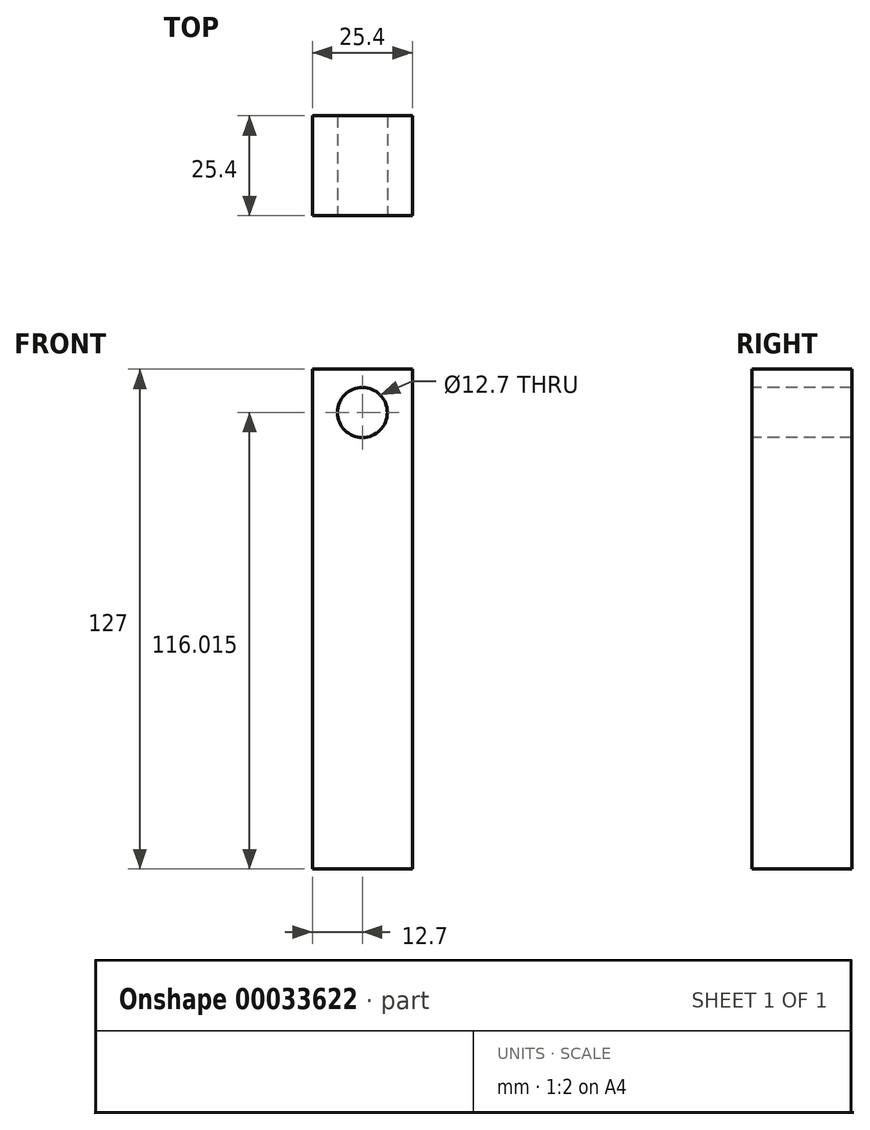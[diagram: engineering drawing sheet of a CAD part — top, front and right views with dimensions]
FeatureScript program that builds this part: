
annotation { "Feature Type Name" : "Feature", "Feature Type Description" : "" }
export const myFeature = defineFeature(function(context is Context, id is Id, definition is map)
    precondition{}
    {
        {
            var Q0;
            Q0=qCreatedBy(makeId("Top.planeOp"),FACE);
            var sketch = newSketch(context, id + "F0", { "sketchPlane" : qUnion([Q0])});
            skLineSegment(sketch, "E0.bottom", {"start": v(0, 0) * mm, "end": v(25.4, 0) * mm});
            skLineSegment(sketch, "E0.top", {"start": v(0, 25.4) * mm, "end": v(25.4, 25.4) * mm});
            skLineSegment(sketch, "E0.left", {"start": v(0, 0) * mm, "end": v(0, 25.4) * mm});
            skLineSegment(sketch, "E0.right", {"start": v(25.4, 0) * mm, "end": v(25.4, 25.4) * mm});
            skSolve(sketch);
        }
        {
            var Q0;
            Q0=makeQuery(id+"F0.imprint","IMPRINT",FACE,{"disambiguationData":[TD([[makeQuery(id+"F0.imprint","IMPRINT",EDGE,{"derivedFrom":sQuery(id+"F0.wireOp",EDGE,"E0.bottom")}),1.0]])]});
            extrude(context, id + "F1", {"entities" : qUnion([Q0]), "depth" : 127 * mm});
        }
        {
            var Q0;
            Q0=makeQuery(id+"F1.opExtrude","SWEPT_FACE",FACE,{"disambiguationData":[OSD([sQuery(id+"F0.wireOp",EDGE,"E0.bottom")])]});
            var sketch = newSketch(context, id + "F2", { "sketchPlane" : qUnion([Q0])});
            skCircle(sketch, "E1", {"center": v(12.7, 116.02) * mm, "radius": 6.35 * mm});
            skPoint(sketch, "E1.centerSnap0", {"position": v(12.7, 127) * mm});
            skSolve(sketch);
        }
        {
            var Q0;
            Q0=makeQuery(id+"F2.imprint","IMPRINT",FACE,{"disambiguationData":[TD([[makeQuery(id+"F2.imprint","IMPRINT",EDGE,{"derivedFrom":sQuery(id+"F2.wireOp",EDGE,"E1")}),1.0]])]});
            extrude(context, id + "F3", {"entities" : qUnion([Q0]), "operationType" : NewBodyOperationType.REMOVE, "oppositeDirection" : true, "depth" : 25.4 * mm});
        }
    });
